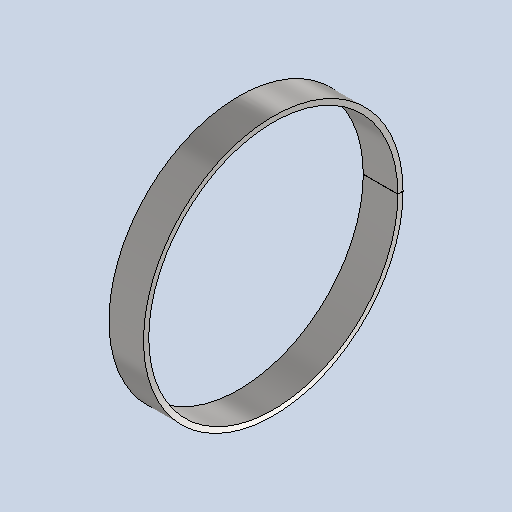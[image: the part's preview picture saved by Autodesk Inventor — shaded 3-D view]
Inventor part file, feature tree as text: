
AUTODESK INVENTOR PART (.ipt)
format: ipt  version: 2025 (Build 290162010, 162A)  size: 134,144 bytes
history: native  units: mm
features: revolve x1, sketch x1, other x1
ambient origin geometry x8: Origin, YZ Plane, XZ Plane, XY Plane, X Axis, Y Axis, Z Axis, Center Point
bodies: Solid1 (feature_tree)
feature tree (3):
  revolve  "Revolution1"  [1 undecoded]
  sketch  "Sketch1"  dims[d2=3.0mm d3=20.0mm d4=75.0mm d5=62.8144mm]
  other  "Definition1"
note: 1 required parameter value undecoded (feature->parameter linkage not recoverable at this tier; creation-order binding heuristic only, values carry confidence <= 0.55)
